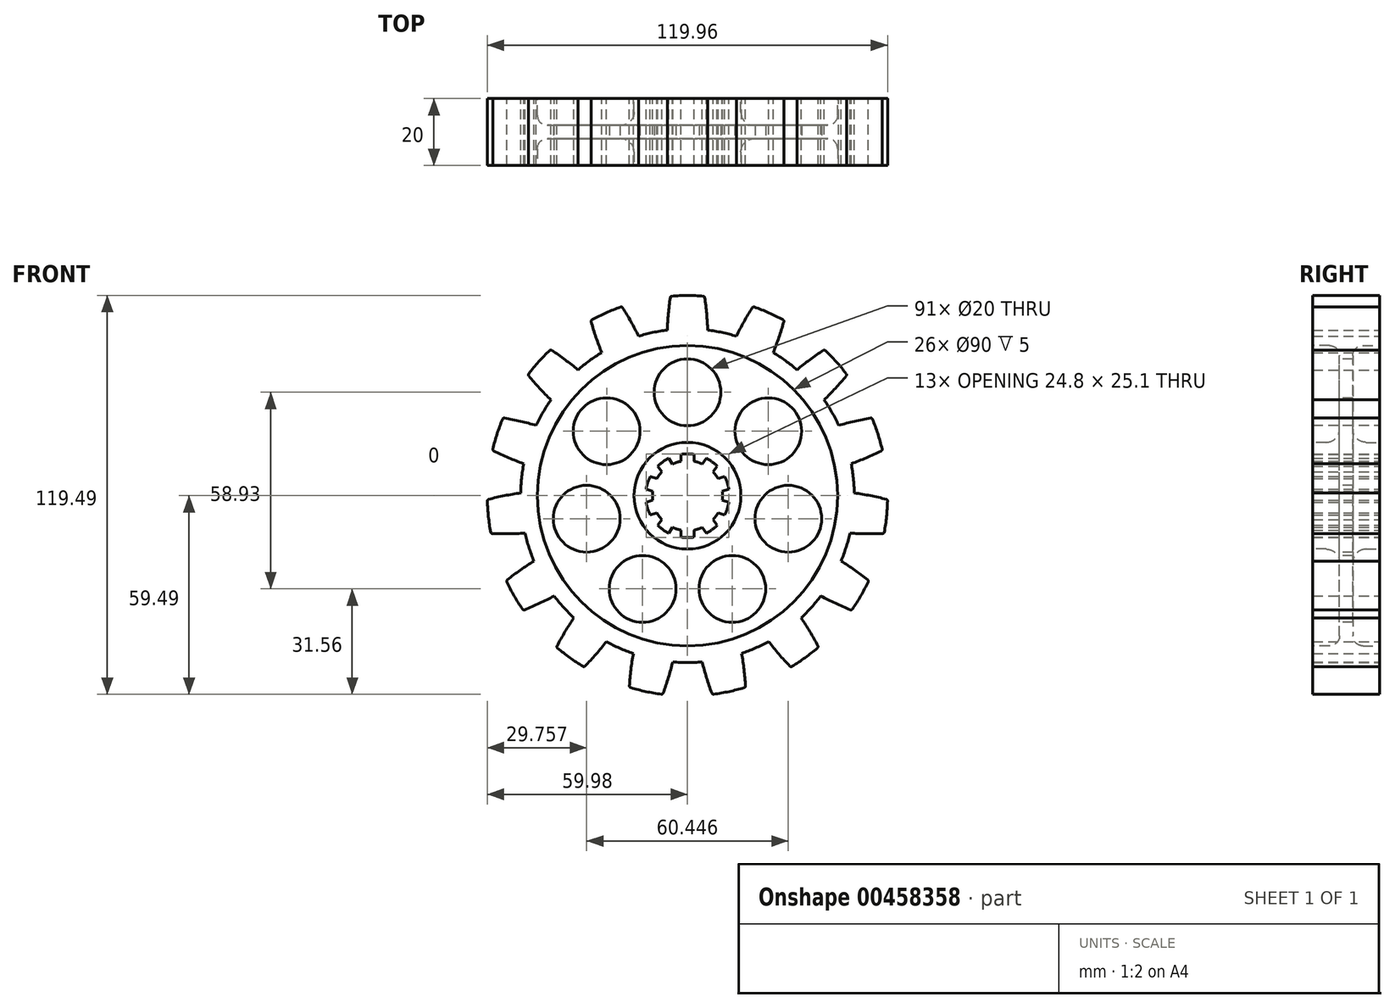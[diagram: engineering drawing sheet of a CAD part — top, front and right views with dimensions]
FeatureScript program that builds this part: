
annotation { "Feature Type Name" : "Feature", "Feature Type Description" : "" }
export const myFeature = defineFeature(function(context is Context, id is Id, definition is map)
    precondition{}
    {
        {
            var Q0;
            Q0=qCreatedBy(makeId("Front.planeOp"),FACE);
            var sketch = newSketch(context, id + "F0", { "sketchPlane" : qUnion([Q0])});
            skCircle(sketch, "E0", {"center": v(0, 0) * mm, "radius": 50 * mm});
            skArc(sketch, "E1", {"start": v(-5.11, 59.78) * mm, "mid": v(-5.72, 54.72) * mm, "end": v(-6.05, 49.63) * mm});
            skArc(sketch, "E2.trimOffspring", {"start": v(5.11, 59.78) * mm, "mid": v(0, 60) * mm, "end": v(-5.11, 59.78) * mm});
            skArc(sketch, "E3.trimOffspring", {"start": v(6.05, 49.63) * mm, "mid": v(5.72, 54.72) * mm, "end": v(5.11, 59.78) * mm});
            skPoint(sketch, "E4.start.orphan", {"position": v(0, 46.5) * mm});
            skArc(sketch, "E5.1.0", {"start": v(-19.64, 56.7) * mm, "mid": v(-24.4, 54.81) * mm, "end": v(-28.99, 52.53) * mm});
            skArc(sketch, "E5.1.1", {"start": v(-14.66, 47.8) * mm, "mid": v(-17.03, 52.32) * mm, "end": v(-19.64, 56.7) * mm});
            skArc(sketch, "E5.1.2", {"start": v(-28.99, 52.53) * mm, "mid": v(-27.49, 47.66) * mm, "end": v(-25.71, 42.88) * mm});
            skArc(sketch, "E5.2.0", {"start": v(-41, 43.8) * mm, "mid": v(-44.59, 40.15) * mm, "end": v(-47.85, 36.2) * mm});
            skArc(sketch, "E5.2.1", {"start": v(-32.84, 37.7) * mm, "mid": v(-36.84, 40.87) * mm, "end": v(-41, 43.8) * mm});
            skArc(sketch, "E5.2.2", {"start": v(-47.85, 36.2) * mm, "mid": v(-44.5, 32.36) * mm, "end": v(-40.93, 28.72) * mm});
            skArc(sketch, "E6.3.3.0", {"start": v(-55.28, 23.34) * mm, "mid": v(-57.06, 18.54) * mm, "end": v(-58.44, 13.6) * mm});
            skArc(sketch, "E6.4.3.0", {"start": v(-45.34, 21.09) * mm, "mid": v(-50.27, 22.35) * mm, "end": v(-55.28, 23.34) * mm});
            skArc(sketch, "E6.8.3.0", {"start": v(-58.44, 13.6) * mm, "mid": v(-53.81, 11.47) * mm, "end": v(-49.07, 9.59) * mm});
            skArc(sketch, "E6.3.4.0", {"start": v(-59.99, -1.16) * mm, "mid": v(-59.67, -6.27) * mm, "end": v(-58.92, -11.34) * mm});
            skArc(sketch, "E6.4.4.0", {"start": v(-50, 0.82) * mm, "mid": v(-55.02, -0.03) * mm, "end": v(-59.99, -1.16) * mm});
            skArc(sketch, "E6.8.4.0", {"start": v(-58.92, -11.34) * mm, "mid": v(-53.82, -11.41) * mm, "end": v(-48.73, -11.2) * mm});
            skArc(sketch, "E6.3.5.0", {"start": v(-54.33, -25.46) * mm, "mid": v(-51.96, -30) * mm, "end": v(-49.22, -34.32) * mm});
            skArc(sketch, "E6.4.5.0", {"start": v(-46, -19.58) * mm, "mid": v(-50.25, -22.4) * mm, "end": v(-54.33, -25.46) * mm});
            skArc(sketch, "E6.8.5.0", {"start": v(-49.22, -34.32) * mm, "mid": v(-44.53, -32.32) * mm, "end": v(-39.96, -30.05) * mm});
            skArc(sketch, "E6.3.6.0", {"start": v(-39.28, -45.36) * mm, "mid": v(-35.27, -48.54) * mm, "end": v(-31, -51.37) * mm});
            skArc(sketch, "E6.4.6.0", {"start": v(-34.06, -36.6) * mm, "mid": v(-36.8, -40.9) * mm, "end": v(-39.28, -45.36) * mm});
            skArc(sketch, "E6.8.6.0", {"start": v(-31, -51.37) * mm, "mid": v(-27.53, -47.63) * mm, "end": v(-24.28, -43.7) * mm});
            skArc(sketch, "E6.3.7.0", {"start": v(-17.43, -57.41) * mm, "mid": v(-12.47, -58.69) * mm, "end": v(-7.43, -59.54) * mm});
            skArc(sketch, "E6.4.7.0", {"start": v(-16.23, -47.3) * mm, "mid": v(-16.98, -52.33) * mm, "end": v(-17.43, -57.41) * mm});
            skArc(sketch, "E6.8.7.0", {"start": v(-7.43, -59.54) * mm, "mid": v(-5.78, -54.71) * mm, "end": v(-4.4, -49.8) * mm});
            skArc(sketch, "E6.3.8.0", {"start": v(7.43, -59.54) * mm, "mid": v(12.47, -58.69) * mm, "end": v(17.43, -57.41) * mm});
            skArc(sketch, "E6.4.8.0", {"start": v(4.4, -49.8) * mm, "mid": v(5.78, -54.71) * mm, "end": v(7.43, -59.54) * mm});
            skArc(sketch, "E6.8.8.0", {"start": v(17.43, -57.41) * mm, "mid": v(16.98, -52.33) * mm, "end": v(16.23, -47.3) * mm});
            skArc(sketch, "E6.3.9.0", {"start": v(31, -51.37) * mm, "mid": v(35.27, -48.54) * mm, "end": v(39.28, -45.36) * mm});
            skArc(sketch, "E6.4.9.0", {"start": v(24.28, -43.7) * mm, "mid": v(27.53, -47.63) * mm, "end": v(31, -51.37) * mm});
            skArc(sketch, "E6.8.9.0", {"start": v(39.28, -45.36) * mm, "mid": v(36.8, -40.9) * mm, "end": v(34.06, -36.6) * mm});
            skArc(sketch, "E7", {"start": v(-7.68, 7.16) * mm, "mid": v(-8.5, 6.17) * mm, "end": v(-9.19, 5.09) * mm});
            skArc(sketch, "E8", {"start": v(2, 12.39) * mm, "mid": v(0, 12.55) * mm, "end": v(-2, 12.39) * mm});
            skLineSegment(sketch, "E9.left", {"start": v(2, 12.39) * mm, "end": v(2, 10.3) * mm});
            skLineSegment(sketch, "E9.right", {"start": v(-2, 12.39) * mm, "end": v(-2, 10.3) * mm});
            skPoint(sketch, "E10.orphan", {"position": v(-2, 13) * mm});
            skPoint(sketch, "E11.orphan", {"position": v(2, 13) * mm});
            skPoint(sketch, "E12.trimOffspring.end.orphan", {"position": v(2, -13) * mm});
            skPoint(sketch, "E13.trimOffspring.end.orphan", {"position": v(-2, -13) * mm});
            skArc(sketch, "E14.1.0", {"start": v(-5.66, 11.2) * mm, "mid": v(-7.38, 10.15) * mm, "end": v(-8.9, 8.85) * mm});
            skLineSegment(sketch, "E14.1.1", {"start": v(-8.9, 8.85) * mm, "end": v(-7.68, 7.16) * mm});
            skLineSegment(sketch, "E14.1.2", {"start": v(-5.66, 11.2) * mm, "end": v(-4.44, 9.51) * mm});
            skArc(sketch, "E14.2.0", {"start": v(-11.17, 5.73) * mm, "mid": v(-11.94, 3.88) * mm, "end": v(-12.4, 1.93) * mm});
            skLineSegment(sketch, "E14.2.1", {"start": v(-12.4, 1.93) * mm, "end": v(-10.42, 1.28) * mm});
            skLineSegment(sketch, "E14.2.2", {"start": v(-11.17, 5.73) * mm, "end": v(-9.19, 5.09) * mm});
            skArc(sketch, "E15.3.3.0", {"start": v(-12.4, -1.93) * mm, "mid": v(-11.94, -3.88) * mm, "end": v(-11.17, -5.73) * mm});
            skLineSegment(sketch, "E15.4.3.0", {"start": v(-11.17, -5.73) * mm, "end": v(-9.19, -5.09) * mm});
            skLineSegment(sketch, "E15.7.3.0", {"start": v(-12.4, -1.93) * mm, "end": v(-10.42, -1.28) * mm});
            skArc(sketch, "E15.3.4.0", {"start": v(-8.9, -8.85) * mm, "mid": v(-7.38, -10.15) * mm, "end": v(-5.66, -11.2) * mm});
            skLineSegment(sketch, "E15.4.4.0", {"start": v(-5.66, -11.2) * mm, "end": v(-4.44, -9.51) * mm});
            skLineSegment(sketch, "E15.7.4.0", {"start": v(-8.9, -8.85) * mm, "end": v(-7.68, -7.16) * mm});
            skArc(sketch, "E15.3.5.0", {"start": v(-2, -12.39) * mm, "mid": v(0, -12.55) * mm, "end": v(2, -12.39) * mm});
            skLineSegment(sketch, "E15.4.5.0", {"start": v(2, -12.39) * mm, "end": v(2, -10.3) * mm});
            skLineSegment(sketch, "E15.7.5.0", {"start": v(-2, -12.39) * mm, "end": v(-2, -10.3) * mm});
            skArc(sketch, "E15.3.6.0", {"start": v(5.66, -11.2) * mm, "mid": v(7.38, -10.15) * mm, "end": v(8.9, -8.85) * mm});
            skLineSegment(sketch, "E15.4.6.0", {"start": v(8.9, -8.85) * mm, "end": v(7.68, -7.16) * mm});
            skLineSegment(sketch, "E15.7.6.0", {"start": v(5.66, -11.2) * mm, "end": v(4.44, -9.51) * mm});
            skArc(sketch, "E15.3.7.0", {"start": v(11.17, -5.73) * mm, "mid": v(11.94, -3.88) * mm, "end": v(12.4, -1.93) * mm});
            skLineSegment(sketch, "E15.4.7.0", {"start": v(12.4, -1.93) * mm, "end": v(10.42, -1.28) * mm});
            skLineSegment(sketch, "E15.7.7.0", {"start": v(11.17, -5.73) * mm, "end": v(9.19, -5.09) * mm});
            skArc(sketch, "E15.3.8.0", {"start": v(12.4, 1.93) * mm, "mid": v(11.94, 3.88) * mm, "end": v(11.17, 5.73) * mm});
            skLineSegment(sketch, "E15.4.8.0", {"start": v(11.17, 5.73) * mm, "end": v(9.19, 5.09) * mm});
            skLineSegment(sketch, "E15.7.8.0", {"start": v(12.4, 1.93) * mm, "end": v(10.42, 1.28) * mm});
            skArc(sketch, "E15.3.9.0", {"start": v(8.9, 8.85) * mm, "mid": v(7.38, 10.15) * mm, "end": v(5.66, 11.2) * mm});
            skLineSegment(sketch, "E15.4.9.0", {"start": v(5.66, 11.2) * mm, "end": v(4.44, 9.51) * mm});
            skLineSegment(sketch, "E15.7.9.0", {"start": v(8.9, 8.85) * mm, "end": v(7.68, 7.16) * mm});
            skArc(sketch, "E16.trimOffspring", {"start": v(-2, 10.3) * mm, "mid": v(-3.24, 9.99) * mm, "end": v(-4.44, 9.51) * mm});
            skArc(sketch, "E17.trimOffspring", {"start": v(4.44, 9.51) * mm, "mid": v(3.24, 9.99) * mm, "end": v(2, 10.3) * mm});
            skArc(sketch, "E18.trimOffspring", {"start": v(9.19, 5.09) * mm, "mid": v(8.5, 6.17) * mm, "end": v(7.68, 7.16) * mm});
            skArc(sketch, "E19.trimOffspring", {"start": v(10.42, -1.28) * mm, "mid": v(10.5, 0) * mm, "end": v(10.42, 1.28) * mm});
            skArc(sketch, "E20.trimOffspring", {"start": v(7.68, -7.16) * mm, "mid": v(8.5, -6.17) * mm, "end": v(9.19, -5.09) * mm});
            skArc(sketch, "E21.trimOffspring", {"start": v(2, -10.3) * mm, "mid": v(3.24, -9.99) * mm, "end": v(4.44, -9.51) * mm});
            skArc(sketch, "E22.trimOffspring", {"start": v(-4.44, -9.51) * mm, "mid": v(-3.24, -9.99) * mm, "end": v(-2, -10.3) * mm});
            skArc(sketch, "E23.trimOffspring", {"start": v(-9.19, -5.09) * mm, "mid": v(-8.5, -6.17) * mm, "end": v(-7.68, -7.16) * mm});
            skArc(sketch, "E24.trimOffspring", {"start": v(-10.42, 1.28) * mm, "mid": v(-10.5, 0) * mm, "end": v(-10.42, -1.28) * mm});
            skArc(sketch, "E25.3.10.0", {"start": v(49.22, -34.32) * mm, "mid": v(51.96, -30) * mm, "end": v(54.33, -25.46) * mm});
            skArc(sketch, "E25.4.10.0", {"start": v(39.96, -30.05) * mm, "mid": v(44.53, -32.32) * mm, "end": v(49.22, -34.32) * mm});
            skArc(sketch, "E25.8.10.0", {"start": v(54.33, -25.46) * mm, "mid": v(50.25, -22.4) * mm, "end": v(46, -19.58) * mm});
            skArc(sketch, "E25.3.11.0", {"start": v(58.92, -11.34) * mm, "mid": v(59.67, -6.27) * mm, "end": v(59.99, -1.16) * mm});
            skArc(sketch, "E25.4.11.0", {"start": v(48.73, -11.2) * mm, "mid": v(53.82, -11.41) * mm, "end": v(58.92, -11.34) * mm});
            skArc(sketch, "E25.8.11.0", {"start": v(59.99, -1.16) * mm, "mid": v(55.02, -0.03) * mm, "end": v(50, 0.82) * mm});
            skArc(sketch, "E25.3.12.0", {"start": v(58.44, 13.6) * mm, "mid": v(57.06, 18.54) * mm, "end": v(55.28, 23.34) * mm});
            skArc(sketch, "E25.4.12.0", {"start": v(49.07, 9.59) * mm, "mid": v(53.81, 11.47) * mm, "end": v(58.44, 13.6) * mm});
            skArc(sketch, "E25.8.12.0", {"start": v(55.28, 23.34) * mm, "mid": v(50.27, 22.35) * mm, "end": v(45.34, 21.09) * mm});
            skArc(sketch, "E25.3.13.0", {"start": v(47.85, 36.2) * mm, "mid": v(44.59, 40.15) * mm, "end": v(41, 43.8) * mm});
            skArc(sketch, "E25.4.13.0", {"start": v(40.93, 28.72) * mm, "mid": v(44.5, 32.36) * mm, "end": v(47.85, 36.2) * mm});
            skArc(sketch, "E25.8.13.0", {"start": v(41, 43.8) * mm, "mid": v(36.84, 40.87) * mm, "end": v(32.84, 37.7) * mm});
            skArc(sketch, "E25.3.14.0", {"start": v(28.99, 52.53) * mm, "mid": v(24.4, 54.81) * mm, "end": v(19.64, 56.7) * mm});
            skArc(sketch, "E25.4.14.0", {"start": v(25.71, 42.88) * mm, "mid": v(27.49, 47.66) * mm, "end": v(28.99, 52.53) * mm});
            skArc(sketch, "E25.8.14.0", {"start": v(19.64, 56.7) * mm, "mid": v(17.03, 52.32) * mm, "end": v(14.66, 47.8) * mm});
            skSolve(sketch);
        }
        {
            var Q0;
            Q0=makeQuery(id+"F0.imprint","IMPRINT",FACE,{"disambiguationData":[TD([[makeQuery(id+"F0.imprint","IMPRINT",EDGE,{"derivedFrom":sQuery(id+"F0.wireOp",EDGE,"E6.3.5.0")}),1.0]])]});
            var Q1;
            Q1=makeQuery(id+"F0.imprint","IMPRINT",FACE,{"disambiguationData":[TD([[makeQuery(id+"F0.imprint","IMPRINT",EDGE,{"derivedFrom":sQuery(id+"F0.wireOp",EDGE,"E6.3.7.0")}),1.0]])]});
            var Q2;
            Q2=makeQuery(id+"F0.imprint","IMPRINT",FACE,{"disambiguationData":[TD([[makeQuery(id+"F0.imprint","IMPRINT",EDGE,{"derivedFrom":sQuery(id+"F0.wireOp",EDGE,"E5.2.0")}),1.0]])]});
            var Q3;
            Q3=makeQuery(id+"F0.imprint","IMPRINT",FACE,{"disambiguationData":[TD([[makeQuery(id+"F0.imprint","IMPRINT",EDGE,{"derivedFrom":sQuery(id+"F0.wireOp",EDGE,"E6.3.3.0")}),1.0]])]});
            var Q4;
            Q4=makeQuery(id+"F0.imprint","IMPRINT",FACE,{"disambiguationData":[TD([[makeQuery(id+"F0.imprint","IMPRINT",EDGE,{"derivedFrom":sQuery(id+"F0.wireOp",EDGE,"E6.3.4.0")}),1.0]])]});
            var Q5;
            Q5=makeQuery(id+"F0.imprint","IMPRINT",FACE,{"disambiguationData":[TD([[makeQuery(id+"F0.imprint","IMPRINT",EDGE,{"derivedFrom":sQuery(id+"F0.wireOp",EDGE,"E6.3.6.0")}),1.0]])]});
            var Q6;
            Q6=makeQuery(id+"F0.imprint","IMPRINT",FACE,{"disambiguationData":[TD([[makeQuery(id+"F0.imprint","IMPRINT",EDGE,{"derivedFrom":sQuery(id+"F0.wireOp",EDGE,"E7")}),-1.0]])]});
            var Q7;
            Q7=makeQuery(id+"F0.imprint","IMPRINT",FACE,{"disambiguationData":[TD([[makeQuery(id+"F0.imprint","IMPRINT",EDGE,{"derivedFrom":sQuery(id+"F0.wireOp",EDGE,"E6.3.9.0")}),1.0]])]});
            var Q8;
            Q8=makeQuery(id+"F0.imprint","IMPRINT",FACE,{"disambiguationData":[TD([[makeQuery(id+"F0.imprint","IMPRINT",EDGE,{"derivedFrom":sQuery(id+"F0.wireOp",EDGE,"E5.1.0")}),1.0]])]});
            var Q9;
            Q9=makeQuery(id+"F0.imprint","IMPRINT",FACE,{"disambiguationData":[TD([[makeQuery(id+"F0.imprint","IMPRINT",EDGE,{"derivedFrom":sQuery(id+"F0.wireOp",EDGE,"E6.3.8.0")}),1.0]])]});
            var Q10;
            {var subQ0=sQuery(id+"F0.wireOp",EDGE,"E1");Q10=makeQuery(id+"F0.imprint","IMPRINT",FACE,{"disambiguationData":[TD([[makeQuery(id+"F0.imprint","IMPRINT",EDGE,{"derivedFrom":subQ0}),1.0]])]});}
            var Q11;
            Q11=makeQuery(id+"F0.imprint","IMPRINT",FACE,{"disambiguationData":[TD([[makeQuery(id+"F0.imprint","IMPRINT",EDGE,{"derivedFrom":sQuery(id+"F0.wireOp",EDGE,"E25.3.14.0")}),1.0]])]});
            var Q12;
            Q12=makeQuery(id+"F0.imprint","IMPRINT",FACE,{"disambiguationData":[TD([[makeQuery(id+"F0.imprint","IMPRINT",EDGE,{"derivedFrom":sQuery(id+"F0.wireOp",EDGE,"E25.3.13.0")}),1.0]])]});
            var Q13;
            Q13=makeQuery(id+"F0.imprint","IMPRINT",FACE,{"disambiguationData":[TD([[makeQuery(id+"F0.imprint","IMPRINT",EDGE,{"derivedFrom":sQuery(id+"F0.wireOp",EDGE,"E25.3.12.0")}),1.0]])]});
            var Q14;
            Q14=makeQuery(id+"F0.imprint","IMPRINT",FACE,{"disambiguationData":[TD([[makeQuery(id+"F0.imprint","IMPRINT",EDGE,{"derivedFrom":sQuery(id+"F0.wireOp",EDGE,"E25.3.11.0")}),1.0]])]});
            var Q15;
            Q15=makeQuery(id+"F0.imprint","IMPRINT",FACE,{"disambiguationData":[TD([[makeQuery(id+"F0.imprint","IMPRINT",EDGE,{"derivedFrom":sQuery(id+"F0.wireOp",EDGE,"E25.3.10.0")}),1.0]])]});
            extrude(context, id + "F1", {"entities" : qUnion([Q0, Q1, Q2, Q3, Q4, Q5, Q6, Q7, Q8, Q9, Q10, Q11, Q12, Q13, Q14, Q15]), "depth" : 20 * mm});
        }
        {
            var Q0;
            Q0=makeQuery(id+"F1.opExtrude","CAP_FACE",FACE,{"disambiguationData":[OSD([sQuery(id+"F0.wireOp",EDGE,"E0"),sQuery(id+"F0.wireOp",EDGE,"E1"),sQuery(id+"F0.wireOp",EDGE,"E2.trimOffspring"),sQuery(id+"F0.wireOp",EDGE,"E3.trimOffspring"),sQuery(id+"F0.wireOp",EDGE,"E5.1.0"),sQuery(id+"F0.wireOp",EDGE,"E5.1.1"),sQuery(id+"F0.wireOp",EDGE,"E5.1.2"),sQuery(id+"F0.wireOp",EDGE,"E5.2.0"),sQuery(id+"F0.wireOp",EDGE,"E5.2.1"),sQuery(id+"F0.wireOp",EDGE,"E5.2.2"),sQuery(id+"F0.wireOp",EDGE,"E6.3.3.0"),sQuery(id+"F0.wireOp",EDGE,"E6.4.3.0"),sQuery(id+"F0.wireOp",EDGE,"E6.8.3.0"),sQuery(id+"F0.wireOp",EDGE,"E6.3.4.0"),sQuery(id+"F0.wireOp",EDGE,"E6.4.4.0"),sQuery(id+"F0.wireOp",EDGE,"E6.8.4.0"),sQuery(id+"F0.wireOp",EDGE,"E6.3.5.0"),sQuery(id+"F0.wireOp",EDGE,"E6.4.5.0"),sQuery(id+"F0.wireOp",EDGE,"E6.8.5.0"),sQuery(id+"F0.wireOp",EDGE,"E6.3.6.0"),sQuery(id+"F0.wireOp",EDGE,"E6.4.6.0"),sQuery(id+"F0.wireOp",EDGE,"E6.8.6.0"),sQuery(id+"F0.wireOp",EDGE,"E6.3.7.0"),sQuery(id+"F0.wireOp",EDGE,"E6.4.7.0"),sQuery(id+"F0.wireOp",EDGE,"E6.8.7.0"),sQuery(id+"F0.wireOp",EDGE,"E6.3.8.0"),sQuery(id+"F0.wireOp",EDGE,"E6.4.8.0"),sQuery(id+"F0.wireOp",EDGE,"E6.8.8.0"),sQuery(id+"F0.wireOp",EDGE,"E6.3.9.0"),sQuery(id+"F0.wireOp",EDGE,"E6.4.9.0"),sQuery(id+"F0.wireOp",EDGE,"E6.8.9.0"),sQuery(id+"F0.wireOp",EDGE,"E7"),sQuery(id+"F0.wireOp",EDGE,"E8"),sQuery(id+"F0.wireOp",EDGE,"E9.left"),sQuery(id+"F0.wireOp",EDGE,"E9.right"),sQuery(id+"F0.wireOp",EDGE,"E14.1.0"),sQuery(id+"F0.wireOp",EDGE,"E14.1.1"),sQuery(id+"F0.wireOp",EDGE,"E14.1.2"),sQuery(id+"F0.wireOp",EDGE,"E14.2.0"),sQuery(id+"F0.wireOp",EDGE,"E14.2.1"),sQuery(id+"F0.wireOp",EDGE,"E14.2.2"),sQuery(id+"F0.wireOp",EDGE,"E15.3.3.0"),sQuery(id+"F0.wireOp",EDGE,"E15.4.3.0"),sQuery(id+"F0.wireOp",EDGE,"E15.7.3.0"),sQuery(id+"F0.wireOp",EDGE,"E15.3.4.0"),sQuery(id+"F0.wireOp",EDGE,"E15.4.4.0"),sQuery(id+"F0.wireOp",EDGE,"E15.7.4.0"),sQuery(id+"F0.wireOp",EDGE,"E15.3.5.0"),sQuery(id+"F0.wireOp",EDGE,"E15.4.5.0"),sQuery(id+"F0.wireOp",EDGE,"E15.7.5.0"),sQuery(id+"F0.wireOp",EDGE,"E15.3.6.0"),sQuery(id+"F0.wireOp",EDGE,"E15.4.6.0"),sQuery(id+"F0.wireOp",EDGE,"E15.7.6.0"),sQuery(id+"F0.wireOp",EDGE,"E15.3.7.0"),sQuery(id+"F0.wireOp",EDGE,"E15.4.7.0"),sQuery(id+"F0.wireOp",EDGE,"E15.7.7.0"),sQuery(id+"F0.wireOp",EDGE,"E15.3.8.0"),sQuery(id+"F0.wireOp",EDGE,"E15.4.8.0"),sQuery(id+"F0.wireOp",EDGE,"E15.7.8.0"),sQuery(id+"F0.wireOp",EDGE,"E15.3.9.0"),sQuery(id+"F0.wireOp",EDGE,"E15.4.9.0"),sQuery(id+"F0.wireOp",EDGE,"E15.7.9.0"),sQuery(id+"F0.wireOp",EDGE,"E16.trimOffspring"),sQuery(id+"F0.wireOp",EDGE,"E17.trimOffspring"),sQuery(id+"F0.wireOp",EDGE,"E18.trimOffspring"),sQuery(id+"F0.wireOp",EDGE,"E19.trimOffspring"),sQuery(id+"F0.wireOp",EDGE,"E20.trimOffspring"),sQuery(id+"F0.wireOp",EDGE,"E21.trimOffspring"),sQuery(id+"F0.wireOp",EDGE,"E22.trimOffspring"),sQuery(id+"F0.wireOp",EDGE,"E23.trimOffspring"),sQuery(id+"F0.wireOp",EDGE,"E24.trimOffspring"),sQuery(id+"F0.wireOp",EDGE,"E25.3.10.0"),sQuery(id+"F0.wireOp",EDGE,"E25.4.10.0"),sQuery(id+"F0.wireOp",EDGE,"E25.8.10.0"),sQuery(id+"F0.wireOp",EDGE,"E25.3.11.0"),sQuery(id+"F0.wireOp",EDGE,"E25.4.11.0"),sQuery(id+"F0.wireOp",EDGE,"E25.8.11.0"),sQuery(id+"F0.wireOp",EDGE,"E25.3.12.0"),sQuery(id+"F0.wireOp",EDGE,"E25.4.12.0"),sQuery(id+"F0.wireOp",EDGE,"E25.8.12.0"),sQuery(id+"F0.wireOp",EDGE,"E25.3.13.0"),sQuery(id+"F0.wireOp",EDGE,"E25.4.13.0"),sQuery(id+"F0.wireOp",EDGE,"E25.8.13.0"),sQuery(id+"F0.wireOp",EDGE,"E25.3.14.0"),sQuery(id+"F0.wireOp",EDGE,"E25.4.14.0"),sQuery(id+"F0.wireOp",EDGE,"E25.8.14.0")])],"isStart":false});
            var sketch = newSketch(context, id + "F2", { "sketchPlane" : qUnion([Q0])});
            skCircle(sketch, "E26", {"center": v(0, 31) * mm, "radius": 10 * mm});
            skCircle(sketch, "E27.1.0", {"center": v(-24.24, 19.33) * mm, "radius": 10 * mm});
            skCircle(sketch, "E27.2.0", {"center": v(-30.22, -6.9) * mm, "radius": 10 * mm});
            skCircle(sketch, "E27.3.0", {"center": v(-13.45, -27.93) * mm, "radius": 10 * mm});
            skCircle(sketch, "E27.4.0", {"center": v(13.45, -27.93) * mm, "radius": 10 * mm});
            skCircle(sketch, "E27.5.0", {"center": v(30.22, -6.9) * mm, "radius": 10 * mm});
            skCircle(sketch, "E27.6.0", {"center": v(24.24, 19.33) * mm, "radius": 10 * mm});
            skPoint(sketch, "E27.center", {"position": v(0, 0) * mm});
            skSolve(sketch);
        }
        {
            var Q0;
            Q0=makeQuery(id+"F2.imprint","IMPRINT",FACE,{"disambiguationData":[TD([[makeQuery(id+"F2.imprint","IMPRINT",EDGE,{"derivedFrom":sQuery(id+"F2.wireOp",EDGE,"E27.1.0")}),1.0]])]});
            var Q1;
            Q1=makeQuery(id+"F2.imprint","IMPRINT",FACE,{"disambiguationData":[TD([[makeQuery(id+"F2.imprint","IMPRINT",EDGE,{"derivedFrom":sQuery(id+"F2.wireOp",EDGE,"E26")}),1.0]])]});
            var Q2;
            Q2=makeQuery(id+"F2.imprint","IMPRINT",FACE,{"disambiguationData":[TD([[makeQuery(id+"F2.imprint","IMPRINT",EDGE,{"derivedFrom":sQuery(id+"F2.wireOp",EDGE,"E27.6.0")}),1.0]])]});
            var Q3;
            Q3=makeQuery(id+"F2.imprint","IMPRINT",FACE,{"disambiguationData":[TD([[makeQuery(id+"F2.imprint","IMPRINT",EDGE,{"derivedFrom":sQuery(id+"F2.wireOp",EDGE,"E27.5.0")}),1.0]])]});
            var Q4;
            Q4=makeQuery(id+"F2.imprint","IMPRINT",FACE,{"disambiguationData":[TD([[makeQuery(id+"F2.imprint","IMPRINT",EDGE,{"derivedFrom":sQuery(id+"F2.wireOp",EDGE,"E27.4.0")}),1.0]])]});
            var Q5;
            Q5=makeQuery(id+"F2.imprint","IMPRINT",FACE,{"disambiguationData":[TD([[makeQuery(id+"F2.imprint","IMPRINT",EDGE,{"derivedFrom":sQuery(id+"F2.wireOp",EDGE,"E27.3.0")}),1.0]])]});
            var Q6;
            Q6=makeQuery(id+"F2.imprint","IMPRINT",FACE,{"disambiguationData":[TD([[makeQuery(id+"F2.imprint","IMPRINT",EDGE,{"derivedFrom":sQuery(id+"F2.wireOp",EDGE,"E27.2.0")}),1.0]])]});
            var Q7;
            Q7=sQuery(id+"F2.wireOp",EDGE,"E27.1.0");
            var Q8;
            Q8=sQuery(id+"F2.wireOp",EDGE,"E26");
            var Q9;
            Q9=sQuery(id+"F2.wireOp",EDGE,"E27.6.0");
            var Q10;
            Q10=sQuery(id+"F2.wireOp",EDGE,"E27.5.0");
            var Q11;
            Q11=sQuery(id+"F2.wireOp",EDGE,"E27.4.0");
            var Q12;
            Q12=sQuery(id+"F2.wireOp",EDGE,"E27.3.0");
            var Q13;
            Q13=sQuery(id+"F2.wireOp",EDGE,"E27.2.0");
            extrude(context, id + "F3", {"entities" : qUnion([Q0, Q1, Q2, Q3, Q4, Q5, Q6]), "operationType" : NewBodyOperationType.REMOVE, "surfaceEntities" : qUnion([Q7, Q8, Q9, Q10, Q11, Q12, Q13]), "oppositeDirection" : true, "depth" : 25 * mm, "offsetDistance" : 25 * mm});
        }
        {
            var Q0;
            Q0=makeQuery(id+"F1.opExtrude","CAP_FACE",FACE,{"disambiguationData":[OSD([sQuery(id+"F0.wireOp",EDGE,"E0"),sQuery(id+"F0.wireOp",EDGE,"E1"),sQuery(id+"F0.wireOp",EDGE,"E2.trimOffspring"),sQuery(id+"F0.wireOp",EDGE,"E3.trimOffspring"),sQuery(id+"F0.wireOp",EDGE,"E5.1.0"),sQuery(id+"F0.wireOp",EDGE,"E5.1.1"),sQuery(id+"F0.wireOp",EDGE,"E5.1.2"),sQuery(id+"F0.wireOp",EDGE,"E5.2.0"),sQuery(id+"F0.wireOp",EDGE,"E5.2.1"),sQuery(id+"F0.wireOp",EDGE,"E5.2.2"),sQuery(id+"F0.wireOp",EDGE,"E6.3.3.0"),sQuery(id+"F0.wireOp",EDGE,"E6.4.3.0"),sQuery(id+"F0.wireOp",EDGE,"E6.8.3.0"),sQuery(id+"F0.wireOp",EDGE,"E6.3.4.0"),sQuery(id+"F0.wireOp",EDGE,"E6.4.4.0"),sQuery(id+"F0.wireOp",EDGE,"E6.8.4.0"),sQuery(id+"F0.wireOp",EDGE,"E6.3.5.0"),sQuery(id+"F0.wireOp",EDGE,"E6.4.5.0"),sQuery(id+"F0.wireOp",EDGE,"E6.8.5.0"),sQuery(id+"F0.wireOp",EDGE,"E6.3.6.0"),sQuery(id+"F0.wireOp",EDGE,"E6.4.6.0"),sQuery(id+"F0.wireOp",EDGE,"E6.8.6.0"),sQuery(id+"F0.wireOp",EDGE,"E6.3.7.0"),sQuery(id+"F0.wireOp",EDGE,"E6.4.7.0"),sQuery(id+"F0.wireOp",EDGE,"E6.8.7.0"),sQuery(id+"F0.wireOp",EDGE,"E6.3.8.0"),sQuery(id+"F0.wireOp",EDGE,"E6.4.8.0"),sQuery(id+"F0.wireOp",EDGE,"E6.8.8.0"),sQuery(id+"F0.wireOp",EDGE,"E6.3.9.0"),sQuery(id+"F0.wireOp",EDGE,"E6.4.9.0"),sQuery(id+"F0.wireOp",EDGE,"E6.8.9.0"),sQuery(id+"F0.wireOp",EDGE,"E7"),sQuery(id+"F0.wireOp",EDGE,"E8"),sQuery(id+"F0.wireOp",EDGE,"E9.left"),sQuery(id+"F0.wireOp",EDGE,"E9.right"),sQuery(id+"F0.wireOp",EDGE,"E14.1.0"),sQuery(id+"F0.wireOp",EDGE,"E14.1.1"),sQuery(id+"F0.wireOp",EDGE,"E14.1.2"),sQuery(id+"F0.wireOp",EDGE,"E14.2.0"),sQuery(id+"F0.wireOp",EDGE,"E14.2.1"),sQuery(id+"F0.wireOp",EDGE,"E14.2.2"),sQuery(id+"F0.wireOp",EDGE,"E15.3.3.0"),sQuery(id+"F0.wireOp",EDGE,"E15.4.3.0"),sQuery(id+"F0.wireOp",EDGE,"E15.7.3.0"),sQuery(id+"F0.wireOp",EDGE,"E15.3.4.0"),sQuery(id+"F0.wireOp",EDGE,"E15.4.4.0"),sQuery(id+"F0.wireOp",EDGE,"E15.7.4.0"),sQuery(id+"F0.wireOp",EDGE,"E15.3.5.0"),sQuery(id+"F0.wireOp",EDGE,"E15.4.5.0"),sQuery(id+"F0.wireOp",EDGE,"E15.7.5.0"),sQuery(id+"F0.wireOp",EDGE,"E15.3.6.0"),sQuery(id+"F0.wireOp",EDGE,"E15.4.6.0"),sQuery(id+"F0.wireOp",EDGE,"E15.7.6.0"),sQuery(id+"F0.wireOp",EDGE,"E15.3.7.0"),sQuery(id+"F0.wireOp",EDGE,"E15.4.7.0"),sQuery(id+"F0.wireOp",EDGE,"E15.7.7.0"),sQuery(id+"F0.wireOp",EDGE,"E15.3.8.0"),sQuery(id+"F0.wireOp",EDGE,"E15.4.8.0"),sQuery(id+"F0.wireOp",EDGE,"E15.7.8.0"),sQuery(id+"F0.wireOp",EDGE,"E15.3.9.0"),sQuery(id+"F0.wireOp",EDGE,"E15.4.9.0"),sQuery(id+"F0.wireOp",EDGE,"E15.7.9.0"),sQuery(id+"F0.wireOp",EDGE,"E16.trimOffspring"),sQuery(id+"F0.wireOp",EDGE,"E17.trimOffspring"),sQuery(id+"F0.wireOp",EDGE,"E18.trimOffspring"),sQuery(id+"F0.wireOp",EDGE,"E19.trimOffspring"),sQuery(id+"F0.wireOp",EDGE,"E20.trimOffspring"),sQuery(id+"F0.wireOp",EDGE,"E21.trimOffspring"),sQuery(id+"F0.wireOp",EDGE,"E22.trimOffspring"),sQuery(id+"F0.wireOp",EDGE,"E23.trimOffspring"),sQuery(id+"F0.wireOp",EDGE,"E24.trimOffspring"),sQuery(id+"F0.wireOp",EDGE,"E25.3.10.0"),sQuery(id+"F0.wireOp",EDGE,"E25.4.10.0"),sQuery(id+"F0.wireOp",EDGE,"E25.8.10.0"),sQuery(id+"F0.wireOp",EDGE,"E25.3.11.0"),sQuery(id+"F0.wireOp",EDGE,"E25.4.11.0"),sQuery(id+"F0.wireOp",EDGE,"E25.8.11.0"),sQuery(id+"F0.wireOp",EDGE,"E25.3.12.0"),sQuery(id+"F0.wireOp",EDGE,"E25.4.12.0"),sQuery(id+"F0.wireOp",EDGE,"E25.8.12.0"),sQuery(id+"F0.wireOp",EDGE,"E25.3.13.0"),sQuery(id+"F0.wireOp",EDGE,"E25.4.13.0"),sQuery(id+"F0.wireOp",EDGE,"E25.8.13.0"),sQuery(id+"F0.wireOp",EDGE,"E25.3.14.0"),sQuery(id+"F0.wireOp",EDGE,"E25.4.14.0"),sQuery(id+"F0.wireOp",EDGE,"E25.8.14.0")])],"isStart":false});
            var sketch = newSketch(context, id + "F4", { "sketchPlane" : qUnion([Q0])});
            skCircle(sketch, "E28", {"center": v(0, 0) * mm, "radius": 16 * mm});
            skCircle(sketch, "E29", {"center": v(0, 0) * mm, "radius": 45 * mm});
            skSolve(sketch);
        }
        {
            var Q0;
            Q0=makeQuery(id+"F4.imprint","IMPRINT",FACE,{"disambiguationData":[TD([[makeQuery(id+"F4.imprint","IMPRINT",EDGE,{"derivedFrom":sQuery(id+"F4.wireOp",EDGE,"E28")}),-1.0]])]});
            extrude(context, id + "F5", {"entities" : qUnion([Q0]), "operationType" : NewBodyOperationType.REMOVE, "oppositeDirection" : true, "depth" : 8 * mm, "offsetDistance" : 25 * mm});
        }
        {
            var Q0;
            Q0=makeQuery(id+"F1.opExtrude","CAP_FACE",FACE,{"disambiguationData":[OSD([sQuery(id+"F0.wireOp",EDGE,"E0"),sQuery(id+"F0.wireOp",EDGE,"E1"),sQuery(id+"F0.wireOp",EDGE,"E2.trimOffspring"),sQuery(id+"F0.wireOp",EDGE,"E3.trimOffspring"),sQuery(id+"F0.wireOp",EDGE,"E5.1.0"),sQuery(id+"F0.wireOp",EDGE,"E5.1.1"),sQuery(id+"F0.wireOp",EDGE,"E5.1.2"),sQuery(id+"F0.wireOp",EDGE,"E5.2.0"),sQuery(id+"F0.wireOp",EDGE,"E5.2.1"),sQuery(id+"F0.wireOp",EDGE,"E5.2.2"),sQuery(id+"F0.wireOp",EDGE,"E6.3.3.0"),sQuery(id+"F0.wireOp",EDGE,"E6.4.3.0"),sQuery(id+"F0.wireOp",EDGE,"E6.8.3.0"),sQuery(id+"F0.wireOp",EDGE,"E6.3.4.0"),sQuery(id+"F0.wireOp",EDGE,"E6.4.4.0"),sQuery(id+"F0.wireOp",EDGE,"E6.8.4.0"),sQuery(id+"F0.wireOp",EDGE,"E6.3.5.0"),sQuery(id+"F0.wireOp",EDGE,"E6.4.5.0"),sQuery(id+"F0.wireOp",EDGE,"E6.8.5.0"),sQuery(id+"F0.wireOp",EDGE,"E6.3.6.0"),sQuery(id+"F0.wireOp",EDGE,"E6.4.6.0"),sQuery(id+"F0.wireOp",EDGE,"E6.8.6.0"),sQuery(id+"F0.wireOp",EDGE,"E6.3.7.0"),sQuery(id+"F0.wireOp",EDGE,"E6.4.7.0"),sQuery(id+"F0.wireOp",EDGE,"E6.8.7.0"),sQuery(id+"F0.wireOp",EDGE,"E6.3.8.0"),sQuery(id+"F0.wireOp",EDGE,"E6.4.8.0"),sQuery(id+"F0.wireOp",EDGE,"E6.8.8.0"),sQuery(id+"F0.wireOp",EDGE,"E6.3.9.0"),sQuery(id+"F0.wireOp",EDGE,"E6.4.9.0"),sQuery(id+"F0.wireOp",EDGE,"E6.8.9.0"),sQuery(id+"F0.wireOp",EDGE,"E7"),sQuery(id+"F0.wireOp",EDGE,"E8"),sQuery(id+"F0.wireOp",EDGE,"E9.left"),sQuery(id+"F0.wireOp",EDGE,"E9.right"),sQuery(id+"F0.wireOp",EDGE,"E14.1.0"),sQuery(id+"F0.wireOp",EDGE,"E14.1.1"),sQuery(id+"F0.wireOp",EDGE,"E14.1.2"),sQuery(id+"F0.wireOp",EDGE,"E14.2.0"),sQuery(id+"F0.wireOp",EDGE,"E14.2.1"),sQuery(id+"F0.wireOp",EDGE,"E14.2.2"),sQuery(id+"F0.wireOp",EDGE,"E15.3.3.0"),sQuery(id+"F0.wireOp",EDGE,"E15.4.3.0"),sQuery(id+"F0.wireOp",EDGE,"E15.7.3.0"),sQuery(id+"F0.wireOp",EDGE,"E15.3.4.0"),sQuery(id+"F0.wireOp",EDGE,"E15.4.4.0"),sQuery(id+"F0.wireOp",EDGE,"E15.7.4.0"),sQuery(id+"F0.wireOp",EDGE,"E15.3.5.0"),sQuery(id+"F0.wireOp",EDGE,"E15.4.5.0"),sQuery(id+"F0.wireOp",EDGE,"E15.7.5.0"),sQuery(id+"F0.wireOp",EDGE,"E15.3.6.0"),sQuery(id+"F0.wireOp",EDGE,"E15.4.6.0"),sQuery(id+"F0.wireOp",EDGE,"E15.7.6.0"),sQuery(id+"F0.wireOp",EDGE,"E15.3.7.0"),sQuery(id+"F0.wireOp",EDGE,"E15.4.7.0"),sQuery(id+"F0.wireOp",EDGE,"E15.7.7.0"),sQuery(id+"F0.wireOp",EDGE,"E15.3.8.0"),sQuery(id+"F0.wireOp",EDGE,"E15.4.8.0"),sQuery(id+"F0.wireOp",EDGE,"E15.7.8.0"),sQuery(id+"F0.wireOp",EDGE,"E15.3.9.0"),sQuery(id+"F0.wireOp",EDGE,"E15.4.9.0"),sQuery(id+"F0.wireOp",EDGE,"E15.7.9.0"),sQuery(id+"F0.wireOp",EDGE,"E16.trimOffspring"),sQuery(id+"F0.wireOp",EDGE,"E17.trimOffspring"),sQuery(id+"F0.wireOp",EDGE,"E18.trimOffspring"),sQuery(id+"F0.wireOp",EDGE,"E19.trimOffspring"),sQuery(id+"F0.wireOp",EDGE,"E20.trimOffspring"),sQuery(id+"F0.wireOp",EDGE,"E21.trimOffspring"),sQuery(id+"F0.wireOp",EDGE,"E22.trimOffspring"),sQuery(id+"F0.wireOp",EDGE,"E23.trimOffspring"),sQuery(id+"F0.wireOp",EDGE,"E24.trimOffspring"),sQuery(id+"F0.wireOp",EDGE,"E25.3.10.0"),sQuery(id+"F0.wireOp",EDGE,"E25.4.10.0"),sQuery(id+"F0.wireOp",EDGE,"E25.8.10.0"),sQuery(id+"F0.wireOp",EDGE,"E25.3.11.0"),sQuery(id+"F0.wireOp",EDGE,"E25.4.11.0"),sQuery(id+"F0.wireOp",EDGE,"E25.8.11.0"),sQuery(id+"F0.wireOp",EDGE,"E25.3.12.0"),sQuery(id+"F0.wireOp",EDGE,"E25.4.12.0"),sQuery(id+"F0.wireOp",EDGE,"E25.8.12.0"),sQuery(id+"F0.wireOp",EDGE,"E25.3.13.0"),sQuery(id+"F0.wireOp",EDGE,"E25.4.13.0"),sQuery(id+"F0.wireOp",EDGE,"E25.8.13.0"),sQuery(id+"F0.wireOp",EDGE,"E25.3.14.0"),sQuery(id+"F0.wireOp",EDGE,"E25.4.14.0"),sQuery(id+"F0.wireOp",EDGE,"E25.8.14.0")])],"isStart":true});
            var sketch = newSketch(context, id + "F6", { "sketchPlane" : qUnion([Q0])});
            skCircle(sketch, "E30", {"center": v(0, 0) * mm, "radius": 16 * mm});
            skCircle(sketch, "E31", {"center": v(0, 0) * mm, "radius": 45 * mm});
            skSolve(sketch);
        }
        {
            var Q0;
            Q0=makeQuery(id+"F6.imprint","IMPRINT",FACE,{"disambiguationData":[TD([[makeQuery(id+"F6.imprint","IMPRINT",EDGE,{"derivedFrom":sQuery(id+"F6.wireOp",EDGE,"E30")}),-1.0]])]});
            extrude(context, id + "F7", {"entities" : qUnion([Q0]), "operationType" : NewBodyOperationType.REMOVE, "oppositeDirection" : true, "depth" : 8 * mm, "offsetDistance" : 25 * mm});
        }
        {
            var Q0;
            Q0=makeQuery(id+"F5.boolean.opBoolean","COPY",EDGE,{"derivedFrom":makeQuery(id+"F5.opExtrude","CAP_EDGE",EDGE,{"disambiguationData":[OSD([sQuery(id+"F4.wireOp",EDGE,"E29")])],"isStart":false})});
            var Q1;
            Q1=makeQuery(id+"F7.boolean.opBoolean","COPY",EDGE,{"derivedFrom":makeQuery(id+"F7.opExtrude","CAP_EDGE",EDGE,{"disambiguationData":[OSD([sQuery(id+"F6.wireOp",EDGE,"E31")])],"isStart":false})});
            fillet(context, id + "F8", {"entities" : qUnion([Q0, Q1]), "radius" : 3 * mm, "tangentPropagation" : true, "allowEdgeOverflow" : false});
        }
        {
            var Q0;
            Q0=makeQuery(id+"F5.boolean.opBoolean","COPY",EDGE,{"derivedFrom":makeQuery(id+"F5.opExtrude","CAP_EDGE",EDGE,{"disambiguationData":[OSD([sQuery(id+"F4.wireOp",EDGE,"E28")])],"isStart":false})});
            var Q1;
            Q1=makeQuery(id+"F7.boolean.opBoolean","COPY",EDGE,{"derivedFrom":makeQuery(id+"F7.opExtrude","CAP_EDGE",EDGE,{"disambiguationData":[OSD([sQuery(id+"F6.wireOp",EDGE,"E30")])],"isStart":false})});
            fillet(context, id + "F9", {"entities" : qUnion([Q0, Q1]), "radius" : 4 * mm, "tangentPropagation" : true, "allowEdgeOverflow" : false});
        }
        {
            var Q0;
            Q0=makeQuery(id+"F1.opExtrude","SWEPT_EDGE",EDGE,{"disambiguationData":[OSD([sQuery(id+"F0.wireOp",EDGE,"E1"),sQuery(id+"F0.wireOp",EDGE,"E2.trimOffspring")])]});
            var Q1;
            Q1=makeQuery(id+"F1.opExtrude","SWEPT_EDGE",EDGE,{"disambiguationData":[OSD([sQuery(id+"F0.wireOp",EDGE,"E2.trimOffspring"),sQuery(id+"F0.wireOp",EDGE,"E3.trimOffspring")])]});
            var Q2;
            Q2=makeQuery(id+"F1.opExtrude","SWEPT_EDGE",EDGE,{"disambiguationData":[OSD([sQuery(id+"F0.wireOp",EDGE,"E5.1.0"),sQuery(id+"F0.wireOp",EDGE,"E5.1.1")])]});
            var Q3;
            Q3=makeQuery(id+"F1.opExtrude","SWEPT_EDGE",EDGE,{"disambiguationData":[OSD([sQuery(id+"F0.wireOp",EDGE,"E5.2.0"),sQuery(id+"F0.wireOp",EDGE,"E5.2.1")])]});
            var Q4;
            Q4=makeQuery(id+"F1.opExtrude","SWEPT_EDGE",EDGE,{"disambiguationData":[OSD([sQuery(id+"F0.wireOp",EDGE,"E5.2.0"),sQuery(id+"F0.wireOp",EDGE,"E5.2.2")])]});
            var Q5;
            Q5=makeQuery(id+"F1.opExtrude","SWEPT_EDGE",EDGE,{"disambiguationData":[OSD([sQuery(id+"F0.wireOp",EDGE,"E6.3.3.0"),sQuery(id+"F0.wireOp",EDGE,"E6.4.3.0")])]});
            var Q6;
            Q6=makeQuery(id+"F1.opExtrude","SWEPT_EDGE",EDGE,{"disambiguationData":[OSD([sQuery(id+"F0.wireOp",EDGE,"E6.3.3.0"),sQuery(id+"F0.wireOp",EDGE,"E6.8.3.0")])]});
            var Q7;
            Q7=makeQuery(id+"F1.opExtrude","SWEPT_EDGE",EDGE,{"disambiguationData":[OSD([sQuery(id+"F0.wireOp",EDGE,"E6.3.4.0"),sQuery(id+"F0.wireOp",EDGE,"E6.4.4.0")])]});
            var Q8;
            Q8=makeQuery(id+"F1.opExtrude","SWEPT_EDGE",EDGE,{"disambiguationData":[OSD([sQuery(id+"F0.wireOp",EDGE,"E6.3.4.0"),sQuery(id+"F0.wireOp",EDGE,"E6.8.4.0")])]});
            var Q9;
            Q9=makeQuery(id+"F1.opExtrude","SWEPT_EDGE",EDGE,{"disambiguationData":[OSD([sQuery(id+"F0.wireOp",EDGE,"E6.3.5.0"),sQuery(id+"F0.wireOp",EDGE,"E6.4.5.0")])]});
            var Q10;
            Q10=makeQuery(id+"F1.opExtrude","SWEPT_EDGE",EDGE,{"disambiguationData":[OSD([sQuery(id+"F0.wireOp",EDGE,"E6.3.5.0"),sQuery(id+"F0.wireOp",EDGE,"E6.8.5.0")])]});
            var Q11;
            Q11=makeQuery(id+"F1.opExtrude","SWEPT_EDGE",EDGE,{"disambiguationData":[OSD([sQuery(id+"F0.wireOp",EDGE,"E6.3.6.0"),sQuery(id+"F0.wireOp",EDGE,"E6.4.6.0")])]});
            var Q12;
            Q12=makeQuery(id+"F1.opExtrude","SWEPT_EDGE",EDGE,{"disambiguationData":[OSD([sQuery(id+"F0.wireOp",EDGE,"E6.3.6.0"),sQuery(id+"F0.wireOp",EDGE,"E6.8.6.0")])]});
            var Q13;
            Q13=makeQuery(id+"F1.opExtrude","SWEPT_EDGE",EDGE,{"disambiguationData":[OSD([sQuery(id+"F0.wireOp",EDGE,"E6.3.7.0"),sQuery(id+"F0.wireOp",EDGE,"E6.4.7.0")])]});
            var Q14;
            Q14=makeQuery(id+"F1.opExtrude","SWEPT_EDGE",EDGE,{"disambiguationData":[OSD([sQuery(id+"F0.wireOp",EDGE,"E6.3.7.0"),sQuery(id+"F0.wireOp",EDGE,"E6.8.7.0")])]});
            var Q15;
            Q15=makeQuery(id+"F1.opExtrude","SWEPT_EDGE",EDGE,{"disambiguationData":[OSD([sQuery(id+"F0.wireOp",EDGE,"E25.3.14.0"),sQuery(id+"F0.wireOp",EDGE,"E25.8.14.0")])]});
            var Q16;
            Q16=makeQuery(id+"F1.opExtrude","SWEPT_EDGE",EDGE,{"disambiguationData":[OSD([sQuery(id+"F0.wireOp",EDGE,"E25.3.14.0"),sQuery(id+"F0.wireOp",EDGE,"E25.4.14.0")])]});
            var Q17;
            Q17=makeQuery(id+"F1.opExtrude","SWEPT_EDGE",EDGE,{"disambiguationData":[OSD([sQuery(id+"F0.wireOp",EDGE,"E25.3.13.0"),sQuery(id+"F0.wireOp",EDGE,"E25.8.13.0")])]});
            var Q18;
            Q18=makeQuery(id+"F1.opExtrude","SWEPT_EDGE",EDGE,{"disambiguationData":[OSD([sQuery(id+"F0.wireOp",EDGE,"E25.3.13.0"),sQuery(id+"F0.wireOp",EDGE,"E25.4.13.0")])]});
            var Q19;
            Q19=makeQuery(id+"F1.opExtrude","SWEPT_EDGE",EDGE,{"disambiguationData":[OSD([sQuery(id+"F0.wireOp",EDGE,"E25.3.12.0"),sQuery(id+"F0.wireOp",EDGE,"E25.8.12.0")])]});
            var Q20;
            Q20=makeQuery(id+"F1.opExtrude","SWEPT_EDGE",EDGE,{"disambiguationData":[OSD([sQuery(id+"F0.wireOp",EDGE,"E25.3.12.0"),sQuery(id+"F0.wireOp",EDGE,"E25.4.12.0")])]});
            var Q21;
            Q21=makeQuery(id+"F1.opExtrude","SWEPT_EDGE",EDGE,{"disambiguationData":[OSD([sQuery(id+"F0.wireOp",EDGE,"E25.3.11.0"),sQuery(id+"F0.wireOp",EDGE,"E25.8.11.0")])]});
            var Q22;
            Q22=makeQuery(id+"F1.opExtrude","SWEPT_EDGE",EDGE,{"disambiguationData":[OSD([sQuery(id+"F0.wireOp",EDGE,"E25.3.11.0"),sQuery(id+"F0.wireOp",EDGE,"E25.4.11.0")])]});
            var Q23;
            Q23=makeQuery(id+"F1.opExtrude","SWEPT_EDGE",EDGE,{"disambiguationData":[OSD([sQuery(id+"F0.wireOp",EDGE,"E25.3.10.0"),sQuery(id+"F0.wireOp",EDGE,"E25.8.10.0")])]});
            var Q24;
            Q24=makeQuery(id+"F1.opExtrude","SWEPT_EDGE",EDGE,{"disambiguationData":[OSD([sQuery(id+"F0.wireOp",EDGE,"E25.3.10.0"),sQuery(id+"F0.wireOp",EDGE,"E25.4.10.0")])]});
            var Q25;
            Q25=makeQuery(id+"F1.opExtrude","SWEPT_EDGE",EDGE,{"disambiguationData":[OSD([sQuery(id+"F0.wireOp",EDGE,"E6.3.9.0"),sQuery(id+"F0.wireOp",EDGE,"E6.8.9.0")])]});
            var Q26;
            Q26=makeQuery(id+"F1.opExtrude","SWEPT_EDGE",EDGE,{"disambiguationData":[OSD([sQuery(id+"F0.wireOp",EDGE,"E6.3.9.0"),sQuery(id+"F0.wireOp",EDGE,"E6.4.9.0")])]});
            var Q27;
            Q27=makeQuery(id+"F1.opExtrude","SWEPT_EDGE",EDGE,{"disambiguationData":[OSD([sQuery(id+"F0.wireOp",EDGE,"E6.3.8.0"),sQuery(id+"F0.wireOp",EDGE,"E6.8.8.0")])]});
            var Q28;
            Q28=makeQuery(id+"F1.opExtrude","SWEPT_EDGE",EDGE,{"disambiguationData":[OSD([sQuery(id+"F0.wireOp",EDGE,"E6.3.8.0"),sQuery(id+"F0.wireOp",EDGE,"E6.4.8.0")])]});
            var Q29;
            Q29=makeQuery(id+"F1.opExtrude","SWEPT_EDGE",EDGE,{"disambiguationData":[OSD([sQuery(id+"F0.wireOp",EDGE,"E5.1.0"),sQuery(id+"F0.wireOp",EDGE,"E5.1.2")])]});
            fillet(context, id + "F10", {"entities" : qUnion([Q0, Q1, Q2, Q3, Q4, Q5, Q6, Q7, Q8, Q9, Q10, Q11, Q12, Q13, Q14, Q15, Q16, Q17, Q18, Q19, Q20, Q21, Q22, Q23, Q24, Q25, Q26, Q27, Q28, Q29]), "radius" : 0.5 * mm, "tangentPropagation" : true, "allowEdgeOverflow" : false});
        }
    });
